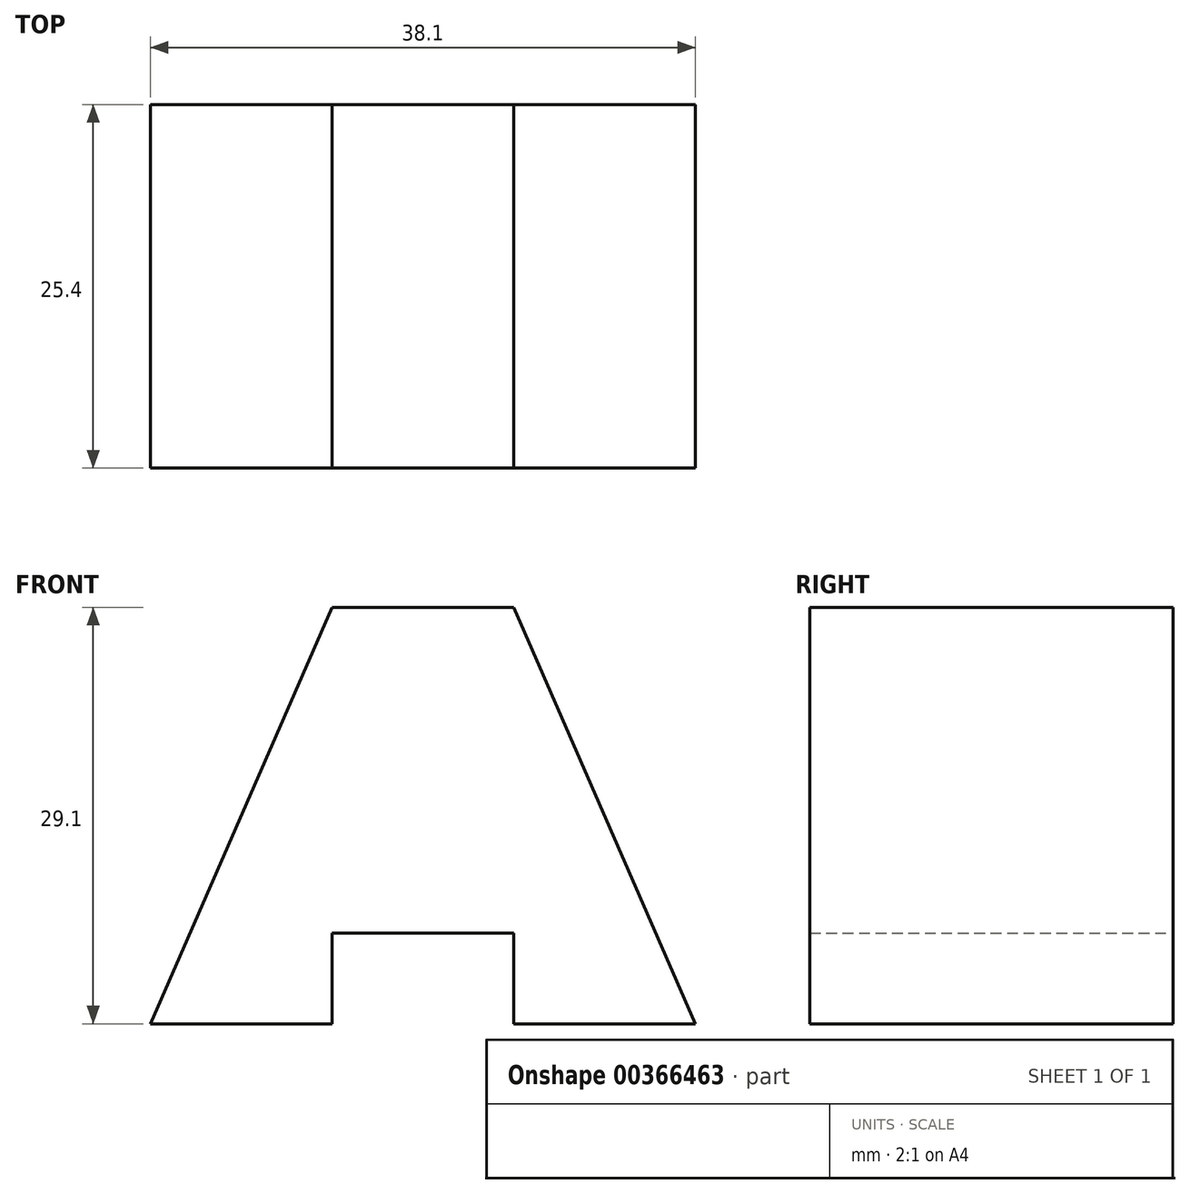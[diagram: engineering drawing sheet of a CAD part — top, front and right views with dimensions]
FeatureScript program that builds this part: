
annotation { "Feature Type Name" : "Feature", "Feature Type Description" : "" }
export const myFeature = defineFeature(function(context is Context, id is Id, definition is map)
    precondition{}
    {
        {
            var Q0;
            Q0=qCreatedBy(makeId("Front.planeOp"),FACE);
            var sketch = newSketch(context, id + "F0", { "sketchPlane" : qUnion([Q0])});
            skLineSegment(sketch, "E0", {"start": v(0, 0) * mm, "end": v(12.7, 0) * mm});
            skLineSegment(sketch, "E1", {"start": v(12.7, 0) * mm, "end": v(12.7, 6.35) * mm});
            skLineSegment(sketch, "E2", {"start": v(12.7, 6.35) * mm, "end": v(25.4, 6.35) * mm});
            skLineSegment(sketch, "E3", {"start": v(25.4, 6.35) * mm, "end": v(25.4, 0) * mm});
            skLineSegment(sketch, "E4", {"start": v(25.4, 0) * mm, "end": v(38.1, 0) * mm});
            skLineSegment(sketch, "E5", {"start": v(38.1, 0) * mm, "end": v(25.4, 29.1) * mm});
            skLineSegment(sketch, "E6", {"start": v(25.4, 29.1) * mm, "end": v(12.7, 29.1) * mm});
            skLineSegment(sketch, "E7", {"start": v(12.7, 29.1) * mm, "end": v(0, 0) * mm});
            skSolve(sketch);
        }
        {
            var Q0;
            Q0 = qSketchRegion(id + "F0", true);
            extrude(context, id + "F1", {"entities" : qUnion([Q0]), "depth" : 25.4 * mm});
        }
    });
